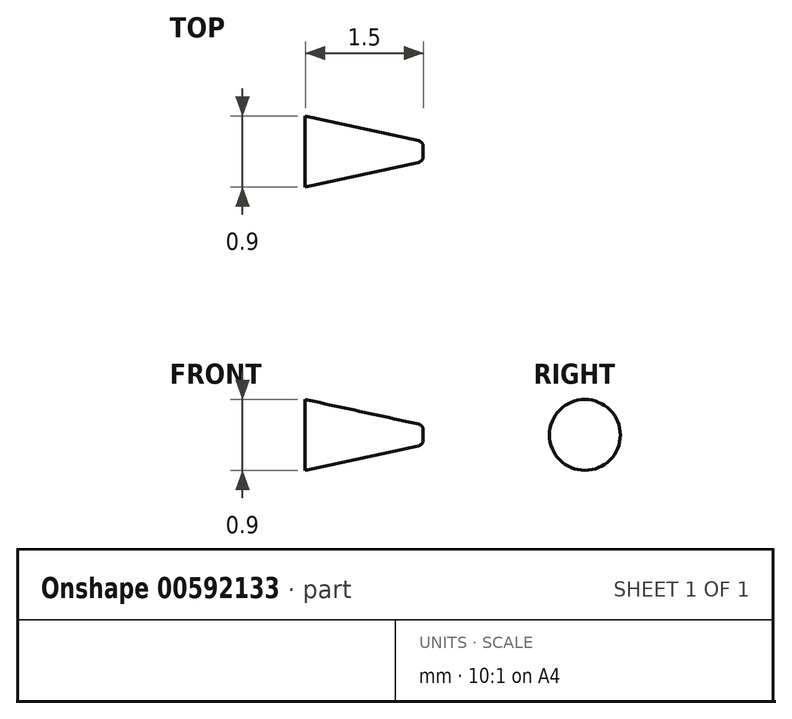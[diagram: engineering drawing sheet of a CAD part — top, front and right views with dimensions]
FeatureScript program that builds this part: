
annotation { "Feature Type Name" : "Feature", "Feature Type Description" : "" }
export const myFeature = defineFeature(function(context is Context, id is Id, definition is map)
    precondition{}
    {
        {
            var Q0;
            Q0=qCreatedBy(makeId("Top.planeOp"),FACE);
            var sketch = newSketch(context, id + "F0", { "sketchPlane" : qUnion([Q0])});
            skCircle(sketch, "E0", {"center": v(0, 0) * mm, "radius": 0.45 * mm});
            skSolve(sketch);
        }
        {
            var Q0;
            Q0=qCreatedBy(makeId("Front.planeOp"),FACE);
            var sketch = newSketch(context, id + "F1", { "sketchPlane" : qUnion([Q0])});
            skLineSegment(sketch, "E1", {"start": v(-1.33, 0) * mm, "end": v(1.67, 0) * mm});
            skLineSegment(sketch, "E2", {"start": v(-1.33, 0) * mm, "end": v(-1.33, 0.9) * mm});
            skLineSegment(sketch, "E3", {"start": v(1.67, 0) * mm, "end": v(1.67, 0.04) * mm});
            skLineSegment(sketch, "E4", {"start": v(1.67, 0) * mm, "end": v(1.67, 0.13) * mm});
            skLineSegment(sketch, "E5", {"start": v(1.55, 0.28) * mm, "end": v(-1.33, 0.9) * mm});
            skPoint(sketch, "E6.visualSharp", {"position": v(1.67, 0.25) * mm});
            skArc(sketch, "E6.filletArc", {"start": v(1.67, 0.13) * mm, "mid": v(1.64, 0.22) * mm, "end": v(1.55, 0.28) * mm});
            skSolve(sketch);
        }
        {
            var Q0;
            Q0 = qSketchRegion(id + "F1", true);
            var Q1;
            Q1=sQuery(id+"F1.wireOp",EDGE,"E1");
            revolve(context, id + "F2", {"entities" : qUnion([Q0]), "axis" : qUnion([Q1]), "revolveType" : RevolveType.FULL});
        }
        {
            var Q0;
            Q0=makeQuery(id+"F2.opRevolve","SWEPT_BODY",BODY,{"disambiguationData":[OSD([sQuery(id+"F1.wireOp",EDGE,"E1"),sQuery(id+"F1.wireOp",EDGE,"E2"),sQuery(id+"F1.wireOp",EDGE,"E4"),sQuery(id+"F1.wireOp",EDGE,"E5"),sQuery(id+"F1.wireOp",EDGE,"E6.filletArc")])]});
            var Q1;
            Q1=sQuery(id+"F0.wireOp",VERTEX,"E0.center");
            transform(context, id + "F3", {"entities" : qUnion([Q0]), "transformType" : TransformType.SCALE_UNIFORMLY, "scale" : .5, "scalePoint" : qUnion([Q1]), "makeCopy" : false});
        }
    });
